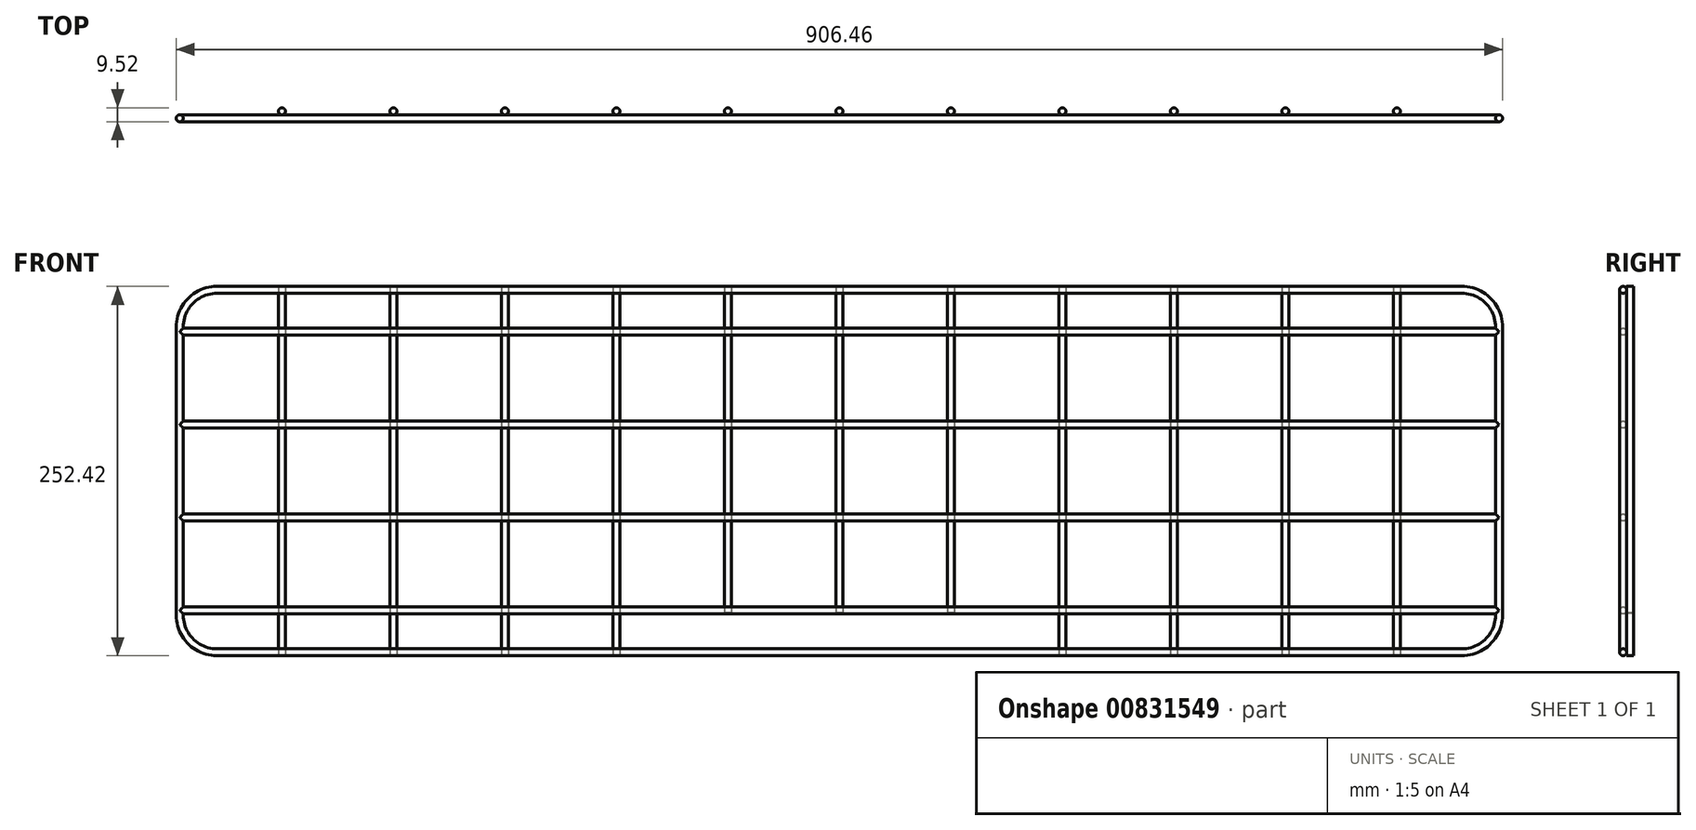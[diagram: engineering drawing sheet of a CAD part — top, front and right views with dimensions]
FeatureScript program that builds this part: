
annotation { "Feature Type Name" : "Feature", "Feature Type Description" : "" }
export const myFeature = defineFeature(function(context is Context, id is Id, definition is map)
    precondition{}
    {
        {
            var Q0;
            Q0=qCreatedBy(makeId("Front.planeOp"),FACE);
            var sketch = newSketch(context, id + "F0", { "sketchPlane" : qUnion([Q0])});
            skLineSegment(sketch, "E0.bottom", {"start": v(-425.45, 123.83) * mm, "end": v(425.45, 123.82) * mm});
            skLineSegment(sketch, "E0.top", {"start": v(-425.45, -123.82) * mm, "end": v(425.45, -123.83) * mm});
            skLineSegment(sketch, "E0.left", {"start": v(-450.85, 98.43) * mm, "end": v(-450.85, -98.43) * mm});
            skLineSegment(sketch, "E0.right", {"start": v(450.85, 98.43) * mm, "end": v(450.85, -98.43) * mm});
            skLineSegment(sketch, "E1", {"start": v(-450.85, 0) * mm, "end": v(0, 0) * mm, "construction": true});
            skLineSegment(sketch, "E2", {"start": v(0, 0) * mm, "end": v(0, 123.83) * mm, "construction": true});
            skPoint(sketch, "E3.visualSharp", {"position": v(-450.85, 123.83) * mm});
            skArc(sketch, "E3.filletArc", {"start": v(-425.45, 123.83) * mm, "mid": v(-443.41, 116.39) * mm, "end": v(-450.85, 98.43) * mm});
            skPoint(sketch, "E4.visualSharp", {"position": v(450.85, 123.82) * mm});
            skArc(sketch, "E4.filletArc", {"start": v(450.85, 98.43) * mm, "mid": v(443.41, 116.39) * mm, "end": v(425.45, 123.83) * mm});
            skPoint(sketch, "E5.visualSharp", {"position": v(450.85, -123.83) * mm});
            skArc(sketch, "E5.filletArc", {"start": v(425.45, -123.83) * mm, "mid": v(443.41, -116.39) * mm, "end": v(450.85, -98.43) * mm});
            skPoint(sketch, "E6.visualSharp", {"position": v(-450.85, -123.82) * mm});
            skArc(sketch, "E6.filletArc", {"start": v(-450.85, -98.43) * mm, "mid": v(-443.41, -116.39) * mm, "end": v(-425.45, -123.83) * mm});
            skSolve(sketch);
        }
        {
            var Q0;
            Q0=qCreatedBy(makeId("Right.planeOp"),FACE);
            var sketch = newSketch(context, id + "F1", { "sketchPlane" : qUnion([Q0])});
            skCircle(sketch, "E7", {"center": v(0, 123.83) * mm, "radius": 2.38 * mm});
            skSolve(sketch);
        }
        {
            var Q0;
            Q0=makeQuery(id+"F1.imprint","IMPRINT",FACE,{"disambiguationData":[TD([[makeQuery(id+"F1.imprint","IMPRINT",EDGE,{"derivedFrom":sQuery(id+"F1.wireOp",EDGE,"E7")}),1.0]])]});
            var Q1;
            Q1=sQuery(id+"F0.wireOp",EDGE,"E0.bottom");
            var Q2;
            Q2=sQuery(id+"F0.wireOp",EDGE,"E3.filletArc");
            var Q3;
            Q3=sQuery(id+"F0.wireOp",EDGE,"E0.left");
            var Q4;
            Q4=sQuery(id+"F0.wireOp",EDGE,"E0.top");
            var Q5;
            Q5=sQuery(id+"F0.wireOp",EDGE,"E6.filletArc");
            var Q6;
            Q6=sQuery(id+"F0.wireOp",EDGE,"E5.filletArc");
            var Q7;
            Q7=sQuery(id+"F0.wireOp",EDGE,"E0.right");
            var Q8;
            Q8=sQuery(id+"F0.wireOp",EDGE,"E4.filletArc");
            sweep(context, id + "F2", {"profiles" : qUnion([Q0]), "path" : qUnion([Q1, Q2, Q3, Q4, Q5, Q6, Q7, Q8])});
        }
        {
            var Q0;
            Q0=qCreatedBy(makeId("Top.planeOp"),FACE);
            var sketch = newSketch(context, id + "F3", { "sketchPlane" : qUnion([Q0])});
            skCircle(sketch, "E8", {"center": v(-381, 4.76) * mm, "radius": 2.38 * mm});
            skCircle(sketch, "E9", {"center": v(-228.6, 4.76) * mm, "radius": 2.38 * mm});
            skCircle(sketch, "E10", {"center": v(152.4, 4.76) * mm, "radius": 2.38 * mm});
            skCircle(sketch, "E11", {"center": v(228.6, 4.76) * mm, "radius": 2.38 * mm});
            skCircle(sketch, "E12", {"center": v(-152.4, 4.76) * mm, "radius": 2.38 * mm});
            skCircle(sketch, "E13", {"center": v(381, 4.76) * mm, "radius": 2.38 * mm});
            skCircle(sketch, "E14", {"center": v(304.8, 4.76) * mm, "radius": 2.38 * mm});
            skCircle(sketch, "E15", {"center": v(-304.8, 4.76) * mm, "radius": 2.38 * mm});
            skLineSegment(sketch, "E16", {"start": v(0, 0) * mm, "end": v(0, 4.76) * mm});
            skCircle(sketch, "E17", {"center": v(-76.2, 4.76) * mm, "radius": 2.38 * mm});
            skCircle(sketch, "E18", {"center": v(76.2, 4.76) * mm, "radius": 2.38 * mm});
            skCircle(sketch, "E19", {"center": v(0, 4.76) * mm, "radius": 2.38 * mm});
            skLineSegment(sketch, "E20", {"start": v(-381, 4.76) * mm, "end": v(-304.8, 4.76) * mm});
            skLineSegment(sketch, "E21", {"start": v(-304.8, 4.76) * mm, "end": v(-228.6, 4.76) * mm});
            skLineSegment(sketch, "E22", {"start": v(-228.6, 4.76) * mm, "end": v(-152.4, 4.76) * mm});
            skLineSegment(sketch, "E23", {"start": v(-152.4, 4.76) * mm, "end": v(-76.2, 4.76) * mm});
            skLineSegment(sketch, "E24", {"start": v(-76.2, 4.76) * mm, "end": v(0, 4.76) * mm});
            skLineSegment(sketch, "E25", {"start": v(0, 4.76) * mm, "end": v(76.2, 4.76) * mm});
            skLineSegment(sketch, "E26", {"start": v(76.2, 4.76) * mm, "end": v(152.4, 4.76) * mm});
            skLineSegment(sketch, "E27", {"start": v(152.4, 4.76) * mm, "end": v(228.6, 4.76) * mm});
            skLineSegment(sketch, "E28", {"start": v(304.8, 4.76) * mm, "end": v(228.6, 4.76) * mm});
            skLineSegment(sketch, "E29", {"start": v(304.8, 4.76) * mm, "end": v(381, 4.76) * mm});
            skSolve(sketch);
        }
        {
            var Q0;
            Q0=makeQuery(id+"F3.imprint","IMPRINT",FACE,{"disambiguationData":[TD([[makeQuery(id+"F3.imprint","IMPRINT",EDGE,{"derivedFrom":sQuery(id+"F3.wireOp",EDGE,"E8")}),1.0]])]});
            var Q1;
            {var subQ0=sQuery(id+"F3.wireOp",EDGE,"E20");var subQ1=sQuery(id+"F3.wireOp",EDGE,"E15");var subQ2=makeQuery(id+"F3.imprint","INTERSECT",VERTEX,{"derivedFrom":[subQ1,subQ0]});Q1=makeQuery(id+"F3.imprint","IMPRINT",FACE,{"disambiguationData":[TD([[makeQuery(id+"F3.imprint","IMPRINT",EDGE,{"disambiguationData":[TD([[subQ2,-1.0]])],"derivedFrom":subQ1}),1.0]])]});}
            var Q2;
            {var subQ0=sQuery(id+"F3.wireOp",EDGE,"E20");var subQ1=sQuery(id+"F3.wireOp",EDGE,"E15");var subQ2=makeQuery(id+"F3.imprint","INTERSECT",VERTEX,{"derivedFrom":[subQ1,subQ0]});Q2=makeQuery(id+"F3.imprint","IMPRINT",FACE,{"disambiguationData":[TD([[makeQuery(id+"F3.imprint","IMPRINT",EDGE,{"disambiguationData":[TD([[subQ2,1.0]])],"derivedFrom":subQ1}),1.0]])]});}
            var Q3;
            {var subQ0=sQuery(id+"F3.wireOp",EDGE,"E21");var subQ1=sQuery(id+"F3.wireOp",EDGE,"E9");var subQ2=makeQuery(id+"F3.imprint","INTERSECT",VERTEX,{"derivedFrom":[subQ1,subQ0]});Q3=makeQuery(id+"F3.imprint","IMPRINT",FACE,{"disambiguationData":[TD([[makeQuery(id+"F3.imprint","IMPRINT",EDGE,{"disambiguationData":[TD([[subQ2,1.0]])],"derivedFrom":subQ1}),1.0]])]});}
            var Q4;
            {var subQ0=sQuery(id+"F3.wireOp",EDGE,"E21");var subQ1=sQuery(id+"F3.wireOp",EDGE,"E9");var subQ2=makeQuery(id+"F3.imprint","INTERSECT",VERTEX,{"derivedFrom":[subQ1,subQ0]});Q4=makeQuery(id+"F3.imprint","IMPRINT",FACE,{"disambiguationData":[TD([[makeQuery(id+"F3.imprint","IMPRINT",EDGE,{"disambiguationData":[TD([[subQ2,-1.0]])],"derivedFrom":subQ1}),1.0]])]});}
            var Q5;
            {var subQ0=sQuery(id+"F3.wireOp",EDGE,"E22");var subQ1=sQuery(id+"F3.wireOp",EDGE,"E12");var subQ2=makeQuery(id+"F3.imprint","INTERSECT",VERTEX,{"derivedFrom":[subQ1,subQ0]});Q5=makeQuery(id+"F3.imprint","IMPRINT",FACE,{"disambiguationData":[TD([[makeQuery(id+"F3.imprint","IMPRINT",EDGE,{"disambiguationData":[TD([[subQ2,1.0]])],"derivedFrom":subQ1}),1.0]])]});}
            var Q6;
            {var subQ0=sQuery(id+"F3.wireOp",EDGE,"E22");var subQ1=sQuery(id+"F3.wireOp",EDGE,"E12");var subQ2=makeQuery(id+"F3.imprint","INTERSECT",VERTEX,{"derivedFrom":[subQ1,subQ0]});Q6=makeQuery(id+"F3.imprint","IMPRINT",FACE,{"disambiguationData":[TD([[makeQuery(id+"F3.imprint","IMPRINT",EDGE,{"disambiguationData":[TD([[subQ2,-1.0]])],"derivedFrom":subQ1}),1.0]])]});}
            var Q7;
            {var subQ0=sQuery(id+"F3.wireOp",EDGE,"E26");var subQ1=sQuery(id+"F3.wireOp",EDGE,"E10");var subQ2=makeQuery(id+"F3.imprint","INTERSECT",VERTEX,{"derivedFrom":[subQ1,subQ0]});Q7=makeQuery(id+"F3.imprint","IMPRINT",FACE,{"disambiguationData":[TD([[makeQuery(id+"F3.imprint","IMPRINT",EDGE,{"disambiguationData":[TD([[subQ2,-1.0]])],"derivedFrom":subQ1}),1.0]])]});}
            var Q8;
            {var subQ0=sQuery(id+"F3.wireOp",EDGE,"E26");var subQ1=sQuery(id+"F3.wireOp",EDGE,"E10");var subQ2=makeQuery(id+"F3.imprint","INTERSECT",VERTEX,{"derivedFrom":[subQ1,subQ0]});Q8=makeQuery(id+"F3.imprint","IMPRINT",FACE,{"disambiguationData":[TD([[makeQuery(id+"F3.imprint","IMPRINT",EDGE,{"disambiguationData":[TD([[subQ2,1.0]])],"derivedFrom":subQ1}),1.0]])]});}
            var Q9;
            {var subQ0=sQuery(id+"F3.wireOp",EDGE,"E27");var subQ1=sQuery(id+"F3.wireOp",EDGE,"E11");var subQ2=makeQuery(id+"F3.imprint","INTERSECT",VERTEX,{"derivedFrom":[subQ1,subQ0]});Q9=makeQuery(id+"F3.imprint","IMPRINT",FACE,{"disambiguationData":[TD([[makeQuery(id+"F3.imprint","IMPRINT",EDGE,{"disambiguationData":[TD([[subQ2,1.0]])],"derivedFrom":subQ1}),1.0]])]});}
            var Q10;
            {var subQ0=sQuery(id+"F3.wireOp",EDGE,"E27");var subQ1=sQuery(id+"F3.wireOp",EDGE,"E11");var subQ2=makeQuery(id+"F3.imprint","INTERSECT",VERTEX,{"derivedFrom":[subQ1,subQ0]});Q10=makeQuery(id+"F3.imprint","IMPRINT",FACE,{"disambiguationData":[TD([[makeQuery(id+"F3.imprint","IMPRINT",EDGE,{"disambiguationData":[TD([[subQ2,-1.0]])],"derivedFrom":subQ1}),1.0]])]});}
            var Q11;
            Q11=makeQuery(id+"F3.imprint","IMPRINT",FACE,{"disambiguationData":[TD([[makeQuery(id+"F3.imprint","IMPRINT",EDGE,{"derivedFrom":sQuery(id+"F3.wireOp",EDGE,"E13")}),1.0]])]});
            var Q12;
            {var subQ0=sQuery(id+"F3.wireOp",EDGE,"E28");var subQ1=sQuery(id+"F3.wireOp",EDGE,"E14");var subQ2=makeQuery(id+"F3.imprint","INTERSECT",VERTEX,{"derivedFrom":[subQ1,subQ0]});Q12=makeQuery(id+"F3.imprint","IMPRINT",FACE,{"disambiguationData":[TD([[makeQuery(id+"F3.imprint","IMPRINT",EDGE,{"disambiguationData":[TD([[subQ2,-1.0]])],"derivedFrom":subQ1}),1.0]])]});}
            var Q13;
            {var subQ0=sQuery(id+"F3.wireOp",EDGE,"E28");var subQ1=sQuery(id+"F3.wireOp",EDGE,"E14");var subQ2=makeQuery(id+"F3.imprint","INTERSECT",VERTEX,{"derivedFrom":[subQ1,subQ0]});Q13=makeQuery(id+"F3.imprint","IMPRINT",FACE,{"disambiguationData":[TD([[makeQuery(id+"F3.imprint","IMPRINT",EDGE,{"disambiguationData":[TD([[subQ2,1.0]])],"derivedFrom":subQ1}),1.0]])]});}
            extrude(context, id + "F4", {"entities" : qUnion([Q0, Q1, Q2, Q3, Q4, Q5, Q6, Q7, Q8, Q9, Q10, Q11, Q12, Q13]), "operationType" : NewBodyOperationType.ADD, "depth" : 126.2 * mm, "offsetDistance" : 25.4 * mm, "hasSecondDirection" : true, "secondDirectionOppositeDirection" : true, "secondDirectionDepth" : 126.2 * mm});
        }
        {
            var Q0;
            Q0=qCreatedBy(makeId("Right.planeOp"),FACE);
            var sketch = newSketch(context, id + "F5", { "sketchPlane" : qUnion([Q0])});
            skCircle(sketch, "E30", {"center": v(0, -31.75) * mm, "radius": 2.38 * mm});
            skCircle(sketch, "E31", {"center": v(0, 31.75) * mm, "radius": 2.38 * mm});
            skCircle(sketch, "E32", {"center": v(0, 95.25) * mm, "radius": 2.38 * mm});
            skCircle(sketch, "E33", {"center": v(0, -95.25) * mm, "radius": 2.38 * mm});
            skLineSegment(sketch, "E34", {"start": v(0, -95.25) * mm, "end": v(0, -31.75) * mm, "construction": true});
            skLineSegment(sketch, "E35", {"start": v(0, 0) * mm, "end": v(0, -31.75) * mm, "construction": true});
            skLineSegment(sketch, "E36", {"start": v(0, 0) * mm, "end": v(0, 31.75) * mm, "construction": true});
            skLineSegment(sketch, "E37", {"start": v(0, 31.75) * mm, "end": v(0, 95.25) * mm, "construction": true});
            skSolve(sketch);
        }
        {
            var Q0;
            Q0 = qSketchRegion(id + "F5", true);
            var Q1;
            Q1=makeQuery(id+"F2.opSweep","SWEPT_FACE",FACE,{"disambiguationData":[OSD([sQuery(id+"F0.wireOp",EDGE,"E0.right"),sQuery(id+"F1.wireOp",EDGE,"E7")])]});
            var Q2;
            Q2=makeQuery(id+"F2.opSweep","SWEPT_FACE",FACE,{"disambiguationData":[OSD([sQuery(id+"F0.wireOp",EDGE,"E0.left"),sQuery(id+"F1.wireOp",EDGE,"E7")])]});
            extrude(context, id + "F6", {"entities" : qUnion([Q0]), "operationType" : NewBodyOperationType.ADD, "endBound" : BoundingType.UP_TO_SURFACE, "depth" : 25.4 * mm, "endBoundEntityFace" : qUnion([Q1]), "offsetDistance" : 25.4 * mm, "hasSecondDirection" : true, "secondDirectionBound" : SecondDirectionBoundingType.UP_TO_SURFACE, "secondDirectionOppositeDirection" : true, "secondDirectionDepth" : 25.4 * mm, "secondDirectionBoundEntityFace" : qUnion([Q2])});
        }
        {
            var Q0;
            {var subQ0=sQuery(id+"F3.wireOp",EDGE,"E23");var subQ1=sQuery(id+"F3.wireOp",EDGE,"E17");var subQ2=makeQuery(id+"F3.imprint","INTERSECT",VERTEX,{"derivedFrom":[subQ1,subQ0]});Q0=makeQuery(id+"F3.imprint","IMPRINT",FACE,{"disambiguationData":[TD([[makeQuery(id+"F3.imprint","IMPRINT",EDGE,{"disambiguationData":[TD([[subQ2,1.0]])],"derivedFrom":subQ1}),1.0]])]});}
            var Q1;
            {var subQ0=sQuery(id+"F3.wireOp",EDGE,"E23");var subQ1=sQuery(id+"F3.wireOp",EDGE,"E17");var subQ2=makeQuery(id+"F3.imprint","INTERSECT",VERTEX,{"derivedFrom":[subQ1,subQ0]});Q1=makeQuery(id+"F3.imprint","IMPRINT",FACE,{"disambiguationData":[TD([[makeQuery(id+"F3.imprint","IMPRINT",EDGE,{"disambiguationData":[TD([[subQ2,-1.0]])],"derivedFrom":subQ1}),1.0]])]});}
            var Q2;
            {var subQ1=sQuery(id+"F3.wireOp",EDGE,"E16");var subQ3=sQuery(id+"F3.wireOp",EDGE,"E19");var subQ4=makeQuery(id+"F3.imprint","INTERSECT",VERTEX,{"derivedFrom":[subQ1,subQ3]});Q2=makeQuery(id+"F3.imprint","IMPRINT",FACE,{"disambiguationData":[TD([[makeQuery(id+"F3.imprint","IMPRINT",EDGE,{"disambiguationData":[TD([[subQ4,1.0]])],"derivedFrom":subQ3}),1.0]])]});}
            var Q3;
            {var subQ0=sQuery(id+"F3.wireOp",EDGE,"E24");var subQ1=sQuery(id+"F3.wireOp",EDGE,"E19");var subQ2=makeQuery(id+"F3.imprint","INTERSECT",VERTEX,{"derivedFrom":[subQ1,subQ0]});Q3=makeQuery(id+"F3.imprint","IMPRINT",FACE,{"disambiguationData":[TD([[makeQuery(id+"F3.imprint","IMPRINT",EDGE,{"disambiguationData":[TD([[subQ2,1.0]])],"derivedFrom":subQ1}),1.0]])]});}
            var Q4;
            {var subQ1=sQuery(id+"F3.wireOp",EDGE,"E16");var subQ3=sQuery(id+"F3.wireOp",EDGE,"E19");var subQ4=makeQuery(id+"F3.imprint","INTERSECT",VERTEX,{"derivedFrom":[subQ1,subQ3]});Q4=makeQuery(id+"F3.imprint","IMPRINT",FACE,{"disambiguationData":[TD([[makeQuery(id+"F3.imprint","IMPRINT",EDGE,{"disambiguationData":[TD([[subQ4,-1.0]])],"derivedFrom":subQ3}),1.0]])]});}
            var Q5;
            {var subQ0=sQuery(id+"F3.wireOp",EDGE,"E25");var subQ1=sQuery(id+"F3.wireOp",EDGE,"E18");var subQ2=makeQuery(id+"F3.imprint","INTERSECT",VERTEX,{"derivedFrom":[subQ1,subQ0]});Q5=makeQuery(id+"F3.imprint","IMPRINT",FACE,{"disambiguationData":[TD([[makeQuery(id+"F3.imprint","IMPRINT",EDGE,{"disambiguationData":[TD([[subQ2,1.0]])],"derivedFrom":subQ1}),1.0]])]});}
            var Q6;
            {var subQ0=sQuery(id+"F3.wireOp",EDGE,"E25");var subQ1=sQuery(id+"F3.wireOp",EDGE,"E18");var subQ2=makeQuery(id+"F3.imprint","INTERSECT",VERTEX,{"derivedFrom":[subQ1,subQ0]});Q6=makeQuery(id+"F3.imprint","IMPRINT",FACE,{"disambiguationData":[TD([[makeQuery(id+"F3.imprint","IMPRINT",EDGE,{"disambiguationData":[TD([[subQ2,-1.0]])],"derivedFrom":subQ1}),1.0]])]});}
            extrude(context, id + "F7", {"entities" : qUnion([Q0, Q1, Q2, Q3, Q4, Q5, Q6]), "depth" : 126.2 * mm, "offsetDistance" : 25.4 * mm, "hasSecondDirection" : true, "secondDirectionOppositeDirection" : true, "secondDirectionDepth" : 96.84 * mm});
        }
    });
